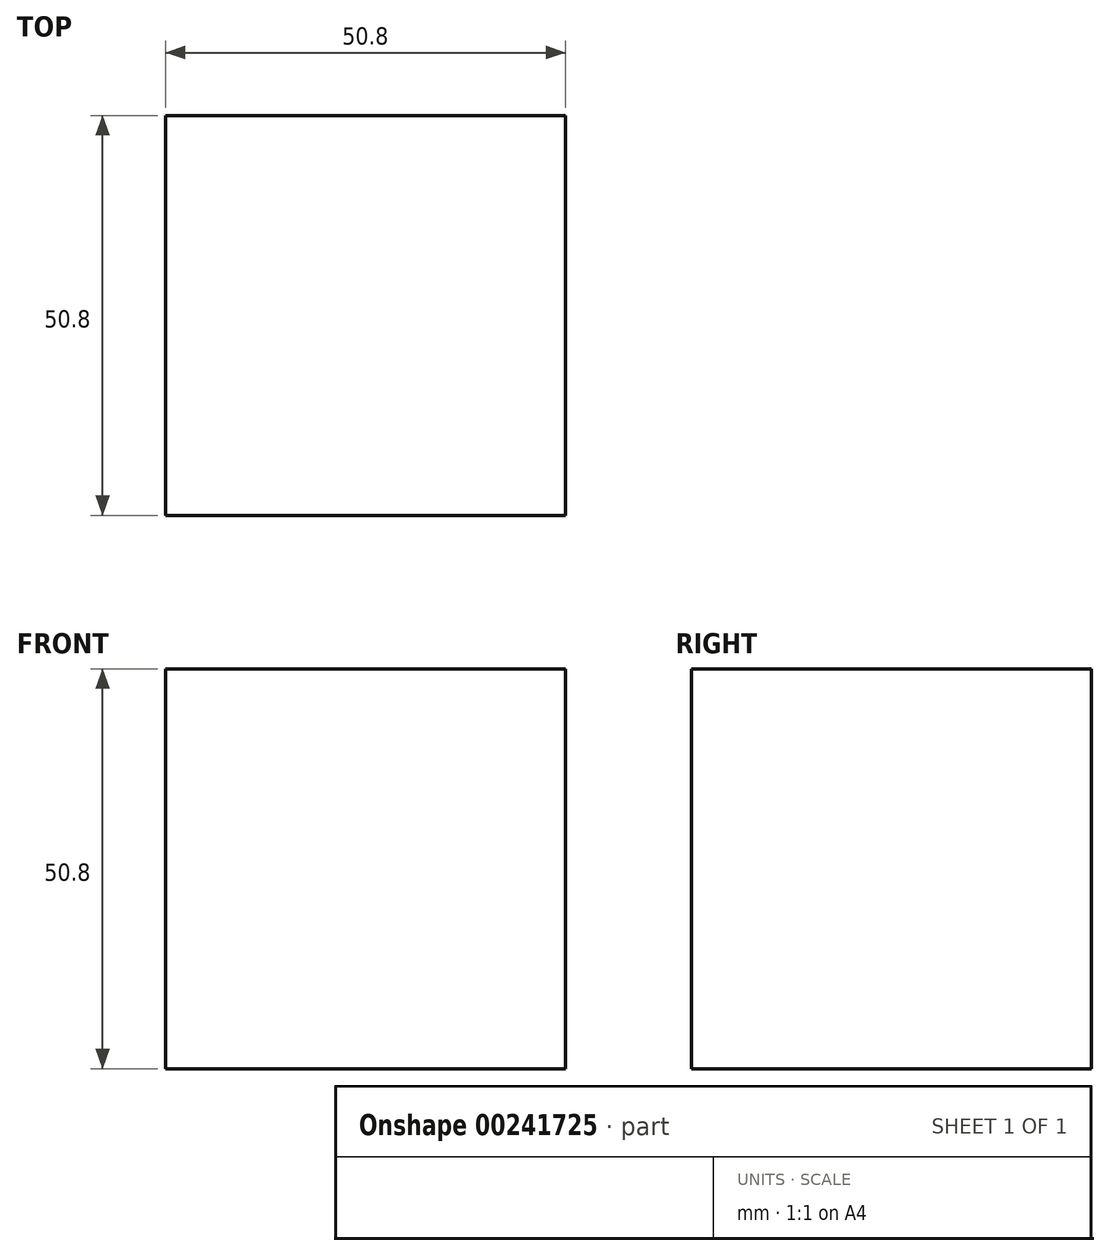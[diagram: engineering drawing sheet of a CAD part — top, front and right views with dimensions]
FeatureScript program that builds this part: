
annotation { "Feature Type Name" : "Feature", "Feature Type Description" : "" }
export const myFeature = defineFeature(function(context is Context, id is Id, definition is map)
    precondition{}
    {
        {
            var Q0;
            Q0=qCreatedBy(makeId("Front.planeOp"),FACE);
            var sketch = newSketch(context, id + "F0", { "sketchPlane" : qUnion([Q0])});
            skLineSegment(sketch, "E0.bottom", {"start": v(25.4, 25.4) * mm, "end": v(-25.4, 25.4) * mm});
            skLineSegment(sketch, "E0.top", {"start": v(25.4, -25.4) * mm, "end": v(-25.4, -25.4) * mm});
            skLineSegment(sketch, "E0.left", {"start": v(25.4, 25.4) * mm, "end": v(25.4, -25.4) * mm});
            skLineSegment(sketch, "E0.right", {"start": v(-25.4, 25.4) * mm, "end": v(-25.4, -25.4) * mm});
            skPoint(sketch, "E0.middle", {"position": v(0, 0) * mm});
            skSolve(sketch);
        }
        {
            var Q0;
            Q0 = qSketchRegion(id + "F0", true);
            extrude(context, id + "F1", {"entities" : qUnion([Q0]), "endBound" : BoundingType.SYMMETRIC, "depth" : 50.8 * mm});
        }
    });
